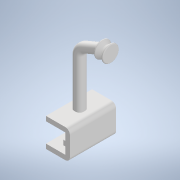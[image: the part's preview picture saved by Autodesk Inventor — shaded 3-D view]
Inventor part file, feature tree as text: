
AUTODESK INVENTOR PART (.ipt)
format: ipt  version: 2021 (Build 250183000, 183)  size: 274,944 bytes
history: native  units: mm
features: extrude x4, other x2, sketch x2, projected_geometry x2, revolve x1, fillet x1, mirror x1
ambient origin geometry x8: Origin, YZ Plane, XZ Plane, XY Plane, X Axis, Y Axis, Z Axis, Center Point
bodies: Body1 (feature_tree)
feature tree (13):
  other  "솔리드1"
  sketch  "스케치1"
  extrude  "돌출1"  Depth=21.0mm
  extrude  "돌출2"  Depth=5.0mm
  revolve  "회전1"
  fillet  "모깎기1"  Radius=50.0mm
  sketch  "스케치2"
  extrude  "돌출3"  Depth=10.0mm TaperAngle=0.0deg
  extrude  "돌출4"  Depth=10.0mm
  other  "작업 평면1"
  mirror  "미러1"
  projected_geometry  "투영된 루프1"
  projected_geometry  "투영된 루프2"
